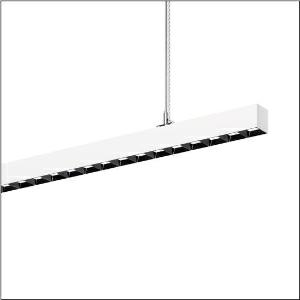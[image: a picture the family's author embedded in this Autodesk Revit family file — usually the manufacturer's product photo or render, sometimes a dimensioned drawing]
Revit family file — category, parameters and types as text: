
# Revit family: silica_r__21_51mx32tctdw_3fbf
name_source: partatom
category: Lighting Fixtures
units: mm (PartAtom-declared; Revit-internal decimal feet)

## family parameters
Cut with Voids When Loaded = No
Host = Face
Light Source = No
Part Type = Normal
Room Calculation Point = No
Round Connector Dimension = Use Diameter
Shared = No

## types (1)
- --- (1 x LED, 15540 lm, 133.6 W, 6500K)
    Apparent Load = 134 VA
    CIE Flux Codes = 84 99 100 60 100
    Color Rendering = 80
    Color Temperature = 6500K
    Default Elevation = 1800 mm
    Description = Silica® 21, office luminaire, primary light control with darklight reflector, of PMMA, black, CAT 2 (L<= 3000cd/m²), light emission: direct/indirect distribution, primary light characteristic: symmetric, installation type: suspended mounting, LED, rated luminous flux: 15.540lm, luminous efficacy: 111lm/W, light colour: 8tw, colour temperature: 2700..6500K, control gear: ECG DALI, with terminal, 3+2-pole, max. 2.5mm², mains connection: 220..240V, AC, 50/60Hz, rated input power: 140.3W, luminaire housing, of aluminium, traffic white (RAL 9016), length: 3.004mm, width: 53mm, height: 53mm, protection rating (complete): IP20, insulation class (complete): insulation class I (protective earthing), certification: CE, permissible operating ambient temperature: 0..+35°C, standard: EN 50419, packaging unit: 1 piece
    Height = 53 mm
    Lamp = 1 x LED
    Lamp Light Flux = 15540 lm
    Lamp Power = 133.6 W
    Lamp count = 1
    Length = 3004 mm
    Luminous efficacy = 116 lm/W
    Manufacturer = Siteco
    ModVariant = No
    Model = 51MX32TCTDW
    Mounting Place = Ceiling
    Mounting Type = Pendant
    Number of Poles = 1
    OnlyDefault = Yes
    Power Factor = 1
    Product Name = Silica® 21
    Product group = office luminaire | ceiling pendant
    ProductGroupID = 902
    Protection Class = Protection class I
    Protection Degree = IP 20
    RLX_Detail_Level = 1
    RLX_Emergency_Light_Flux = 0 lm
    RLX_Emergency_Type = 0
    RLX_Emergency_Type_DB = No
    RlxData = <blob elided: 60525 chars, md5=5690d7e7>
    Socket = socket
    Standby Power = 0 W
    System Light Flux = 15540 lm
    System Power = 134 W
    Type Comments = individual setting
    Type Image = l_1335871.jpg
    URL = http://relux.com
    VarID = @adj_109753
    Voltage = 0 V
    Weight = 0.00 kg
    Width = 53 mm

## geometry (parser evidence)
native form markers: Blend x4, Sweep x15
no freeform markers — native parametric forms only
